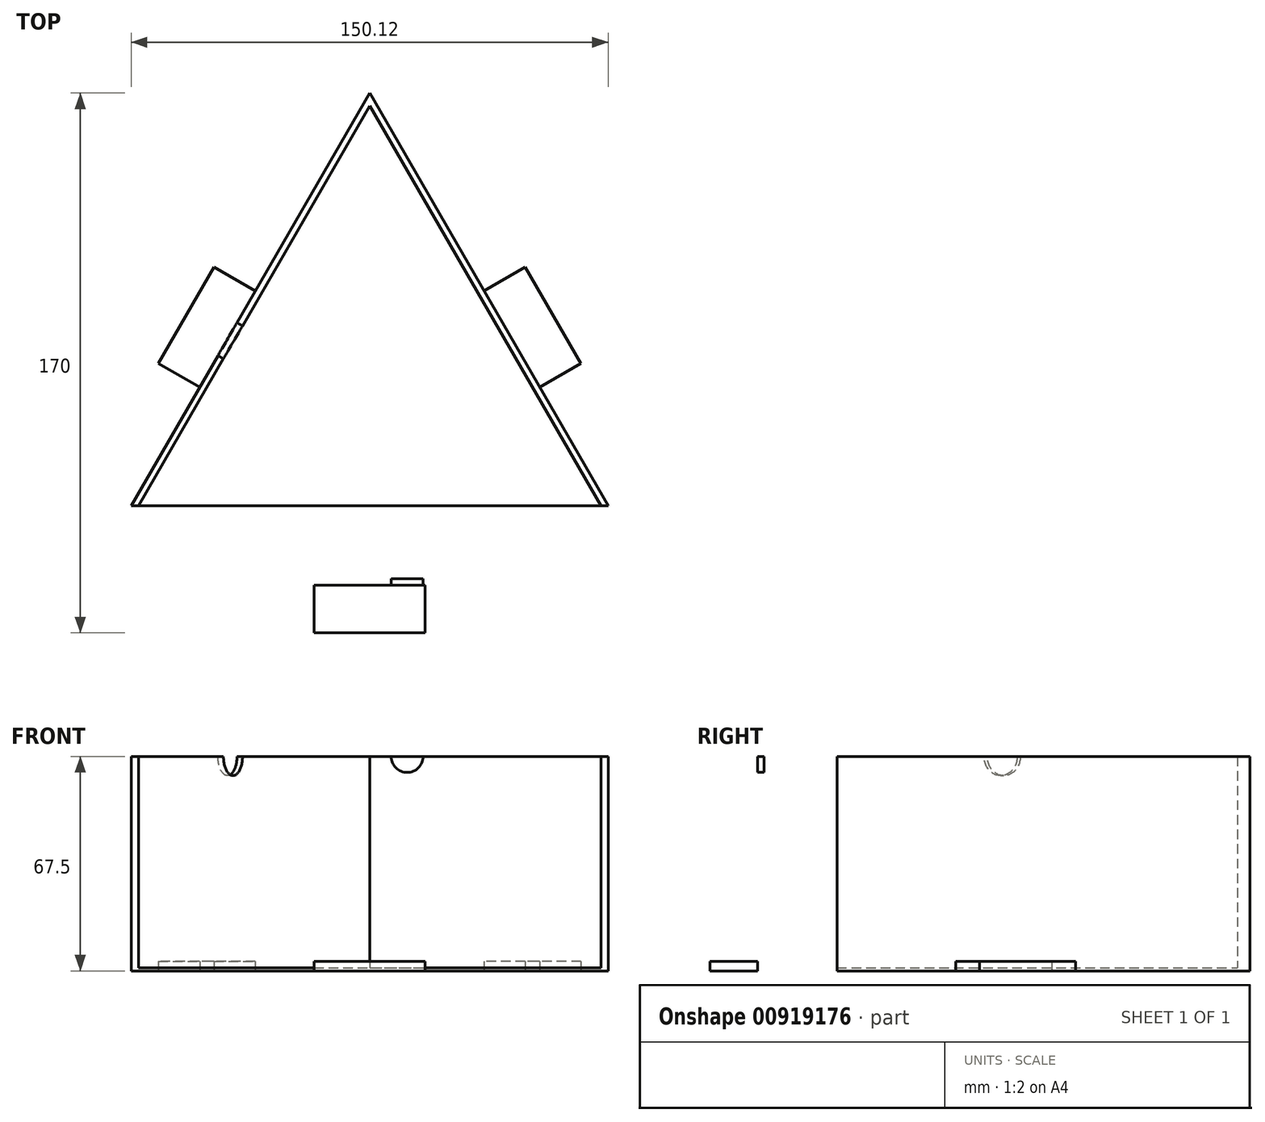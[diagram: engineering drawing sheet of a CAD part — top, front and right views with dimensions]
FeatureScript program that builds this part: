
annotation { "Feature Type Name" : "Feature", "Feature Type Description" : "" }
export const myFeature = defineFeature(function(context is Context, id is Id, definition is map)
    precondition{}
    {
        {
            var Q0;
            Q0=qCreatedBy(makeId("Top.planeOp"),FACE);
            var sketch = newSketch(context, id + "F0", { "sketchPlane" : qUnion([Q0])});
            skCircle(sketch, "E0.cCircle", {"center": v(0, 0) * mm, "radius": 51.67 * mm, "construction": true});
            skLineSegment(sketch, "E0.0", {"start": v(89.49, -51.67) * mm, "end": v(-89.49, -51.67) * mm});
            skLineSegment(sketch, "E0.1", {"start": v(-89.49, -51.67) * mm, "end": v(0, 103.33) * mm});
            skLineSegment(sketch, "E0.2", {"start": v(0, 103.33) * mm, "end": v(89.49, -51.67) * mm});
            skPoint(sketch, "E0.0.midPoint", {"position": v(0, -51.67) * mm});
            skCircle(sketch, "E1.cCircle", {"center": v(0, 0) * mm, "radius": 48.18 * mm, "construction": true});
            skLineSegment(sketch, "E1.0", {"start": v(0, 99.33) * mm, "end": v(86.03, -49.67) * mm});
            skLineSegment(sketch, "E1.1", {"start": v(86.03, -49.67) * mm, "end": v(-86.03, -49.67) * mm});
            skLineSegment(sketch, "E1.2", {"start": v(-86.03, -49.67) * mm, "end": v(0, 99.33) * mm});
            skPoint(sketch, "E1.0.midPoint", {"position": v(0, 48.18) * mm});
            skLineSegment(sketch, "E2", {"start": v(61.46, -7.12) * mm, "end": v(63.2, -6.12) * mm, "construction": true});
            skLineSegment(sketch, "E3", {"start": v(-61.76, -7.64) * mm, "end": v(-63.5, -6.64) * mm, "construction": true});
            skLineSegment(sketch, "E4", {"start": v(-43.91, -49.67) * mm, "end": v(-43.91, -51.67) * mm, "construction": true});
            skLineSegment(sketch, "E5", {"start": v(32.94, -49.67) * mm, "end": v(32.94, -51.67) * mm, "construction": true});
            skLineSegment(sketch, "E6", {"start": v(15.75, 72.05) * mm, "end": v(17.49, 73.05) * mm, "construction": true});
            skLineSegment(sketch, "E7", {"start": v(-20.94, 63.06) * mm, "end": v(-22.67, 64.06) * mm, "construction": true});
            skSolve(sketch);
        }
        {
            var Q0;
            Q0=makeQuery(id+"F0.imprint","IMPRINT",FACE,{"disambiguationData":[TD([[makeQuery(id+"F0.imprint","IMPRINT",EDGE,{"derivedFrom":sQuery(id+"F0.wireOp",EDGE,"E0.0")}),-1.0]])]});
            extrude(context, id + "F1", {"entities" : qUnion([Q0]), "depth" : 67.5 * mm, "offsetDistance" : 25 * mm});
        }
        {
            var Q0;
            Q0=makeQuery(id+"F0.imprint","IMPRINT",FACE,{"disambiguationData":[TD([[makeQuery(id+"F0.imprint","IMPRINT",EDGE,{"derivedFrom":sQuery(id+"F0.wireOp",EDGE,"E1.0")}),-1.0]])]});
            extrude(context, id + "F2", {"entities" : qUnion([Q0]), "operationType" : NewBodyOperationType.ADD, "depth" : 1 * mm, "offsetDistance" : 25 * mm});
        }
        {
            var Q0;
            Q0=makeQuery(id+"F1.opExtrude","SWEPT_FACE",FACE,{"disambiguationData":[OSD([sQuery(id+"F0.wireOp",EDGE,"E0.0")])]});
            var sketch = newSketch(context, id + "F3", { "sketchPlane" : qUnion([Q0])});
            skCircle(sketch, "E8", {"center": v(-11.78, 67.5) * mm, "radius": 5 * mm});
            skLineSegment(sketch, "E9", {"start": v(0, 67.5) * mm, "end": v(0, 0) * mm, "construction": true});
            skCircle(sketch, "E10.MirrorC", {"center": v(11.78, 67.5) * mm, "radius": 5 * mm});
            skSolve(sketch);
        }
        {
            var Q0;
            Q0=makeQuery(id+"F1.opExtrude","SWEPT_FACE",FACE,{"disambiguationData":[OSD([sQuery(id+"F0.wireOp",EDGE,"E0.1")])]});
            var sketch = newSketch(context, id + "F4", { "sketchPlane" : qUnion([Q0])});
            skCircle(sketch, "E11", {"center": v(0, 67.5) * mm, "radius": 6 * mm});
            skSolve(sketch);
        }
        {
            var Q0;
            {var subQ0=sQuery(id+"F4.wireOp",EDGE,"E11");var subQ1=makeQuery(id+"F1.opExtrude","CAP_EDGE",EDGE,{"disambiguationData":[OSD([sQuery(id+"F0.wireOp",EDGE,"E0.1")])],"isStart":false});var subQ2=makeQuery(id+"F4.imprint","INTERSECT",VERTEX,{"disambiguationData":[OD(0.0)],"derivedFrom":[subQ1,subQ0]});Q0=makeQuery(id+"F4.imprint","IMPRINT",FACE,{"disambiguationData":[TD([[makeQuery(id+"F4.imprint","IMPRINT",EDGE,{"disambiguationData":[TD([[subQ2,-1.0]])],"derivedFrom":subQ0}),1.0]])]});}
            var Q1;
            {var subQ0=sQuery(id+"F4.wireOp",EDGE,"E11");var subQ1=makeQuery(id+"F1.opExtrude","CAP_EDGE",EDGE,{"disambiguationData":[OSD([sQuery(id+"F0.wireOp",EDGE,"E0.1")])],"isStart":false});var subQ2=makeQuery(id+"F4.imprint","INTERSECT",VERTEX,{"disambiguationData":[OD(0.0)],"derivedFrom":[subQ1,subQ0]});Q1=makeQuery(id+"F4.imprint","IMPRINT",FACE,{"disambiguationData":[TD([[makeQuery(id+"F4.imprint","IMPRINT",EDGE,{"disambiguationData":[TD([[subQ2,1.0]])],"derivedFrom":subQ0}),1.0]])]});}
            extrude(context, id + "F5", {"entities" : qUnion([Q0, Q1]), "operationType" : NewBodyOperationType.REMOVE, "oppositeDirection" : true, "depth" : 25 * mm, "offsetDistance" : 25 * mm});
        }
        {
            var Q0;
            {var subQ0=sQuery(id+"F3.wireOp",EDGE,"E8");var subQ1=makeQuery(id+"F1.opExtrude","CAP_EDGE",EDGE,{"disambiguationData":[OSD([sQuery(id+"F0.wireOp",EDGE,"E0.0")])],"isStart":false});var subQ2=makeQuery(id+"F3.imprint","INTERSECT",VERTEX,{"disambiguationData":[OD(0.0)],"derivedFrom":[subQ1,subQ0]});Q0=makeQuery(id+"F3.imprint","IMPRINT",FACE,{"disambiguationData":[TD([[makeQuery(id+"F3.imprint","IMPRINT",EDGE,{"disambiguationData":[TD([[subQ2,1.0]])],"derivedFrom":subQ0}),1.0]])]});}
            var Q1;
            {var subQ0=sQuery(id+"F3.wireOp",EDGE,"E8");var subQ1=makeQuery(id+"F1.opExtrude","CAP_EDGE",EDGE,{"disambiguationData":[OSD([sQuery(id+"F0.wireOp",EDGE,"E0.0")])],"isStart":false});var subQ2=makeQuery(id+"F3.imprint","INTERSECT",VERTEX,{"disambiguationData":[OD(0.0)],"derivedFrom":[subQ1,subQ0]});Q1=makeQuery(id+"F3.imprint","IMPRINT",FACE,{"disambiguationData":[TD([[makeQuery(id+"F3.imprint","IMPRINT",EDGE,{"disambiguationData":[TD([[subQ2,-1.0]])],"derivedFrom":subQ0}),1.0]])]});}
            var Q2;
            {var subQ0=sQuery(id+"F3.wireOp",EDGE,"E10.MirrorC");var subQ1=makeQuery(id+"F1.opExtrude","CAP_EDGE",EDGE,{"disambiguationData":[OSD([sQuery(id+"F0.wireOp",EDGE,"E0.0")])],"isStart":false});var subQ2=makeQuery(id+"F3.imprint","INTERSECT",VERTEX,{"disambiguationData":[OD(0.0)],"derivedFrom":[subQ1,subQ0]});Q2=makeQuery(id+"F3.imprint","IMPRINT",FACE,{"disambiguationData":[TD([[makeQuery(id+"F3.imprint","IMPRINT",EDGE,{"disambiguationData":[TD([[subQ2,1.0]])],"derivedFrom":subQ0}),-1.0]])]});}
            var Q3;
            {var subQ0=sQuery(id+"F3.wireOp",EDGE,"E10.MirrorC");var subQ1=makeQuery(id+"F1.opExtrude","CAP_EDGE",EDGE,{"disambiguationData":[OSD([sQuery(id+"F0.wireOp",EDGE,"E0.0")])],"isStart":false});var subQ2=makeQuery(id+"F3.imprint","INTERSECT",VERTEX,{"disambiguationData":[OD(0.0)],"derivedFrom":[subQ1,subQ0]});Q3=makeQuery(id+"F3.imprint","IMPRINT",FACE,{"disambiguationData":[TD([[makeQuery(id+"F3.imprint","IMPRINT",EDGE,{"disambiguationData":[TD([[subQ2,-1.0]])],"derivedFrom":subQ0}),-1.0]])]});}
            extrude(context, id + "F6", {"entities" : qUnion([Q0, Q1, Q2, Q3]), "operationType" : NewBodyOperationType.REMOVE, "oppositeDirection" : true, "depth" : 25 * mm, "offsetDistance" : 25 * mm});
        }
        {
            var Q0;
            Q0=makeQuery(id+"F1.opExtrude","SWEPT_FACE",FACE,{"disambiguationData":[OSD([sQuery(id+"F0.wireOp",EDGE,"E0.0")])]});
            var sketch = newSketch(context, id + "F7", { "sketchPlane" : qUnion([Q0])});
            skLineSegment(sketch, "E12.bottom", {"start": v(-17.5, 3) * mm, "end": v(17.5, 3) * mm});
            skLineSegment(sketch, "E12.top", {"start": v(-17.5, -3) * mm, "end": v(17.5, -3) * mm});
            skLineSegment(sketch, "E12.left", {"start": v(-17.5, 3) * mm, "end": v(-17.5, -3) * mm});
            skLineSegment(sketch, "E12.right", {"start": v(17.5, 3) * mm, "end": v(17.5, -3) * mm});
            skPoint(sketch, "E12.middle", {"position": v(0, 0) * mm});
            skLineSegment(sketch, "E13", {"start": v(-17.5, 0) * mm, "end": v(17.5, 0) * mm});
            skSolve(sketch);
        }
        {
            var Q0;
            {var subQ0=sQuery(id+"F7.wireOp",EDGE,"E12.bottom");Q0=makeQuery(id+"F7.imprint","IMPRINT",FACE,{"disambiguationData":[TD([[makeQuery(id+"F7.imprint","IMPRINT",EDGE,{"derivedFrom":subQ0}),-1.0]])]});}
            extrude(context, id + "F8", {"entities" : qUnion([Q0]), "depth" : 15 * mm, "offsetDistance" : 25 * mm});
        }
        {
            var Q0;
            Q0=makeQuery(id+"F8.opExtrude","SWEPT_BODY",BODY,{"disambiguationData":[OSD([sQuery(id+"F7.wireOp",EDGE,"E12.bottom"),sQuery(id+"F7.wireOp",EDGE,"E12.left"),sQuery(id+"F7.wireOp",EDGE,"E12.right"),sQuery(id+"F7.wireOp",EDGE,"E13")])]});
            var Q1;
            Q1=sQuery(id+"F0.wireOp",EDGE,"E1.cCircle");
            circularPattern(context, id + "F9", {"entities" : qUnion([Q0]), "axis" : qUnion([Q1]), "angle" : 360 * degree, "instanceCount" : 3, "equalSpace" : true});
        }
    });
